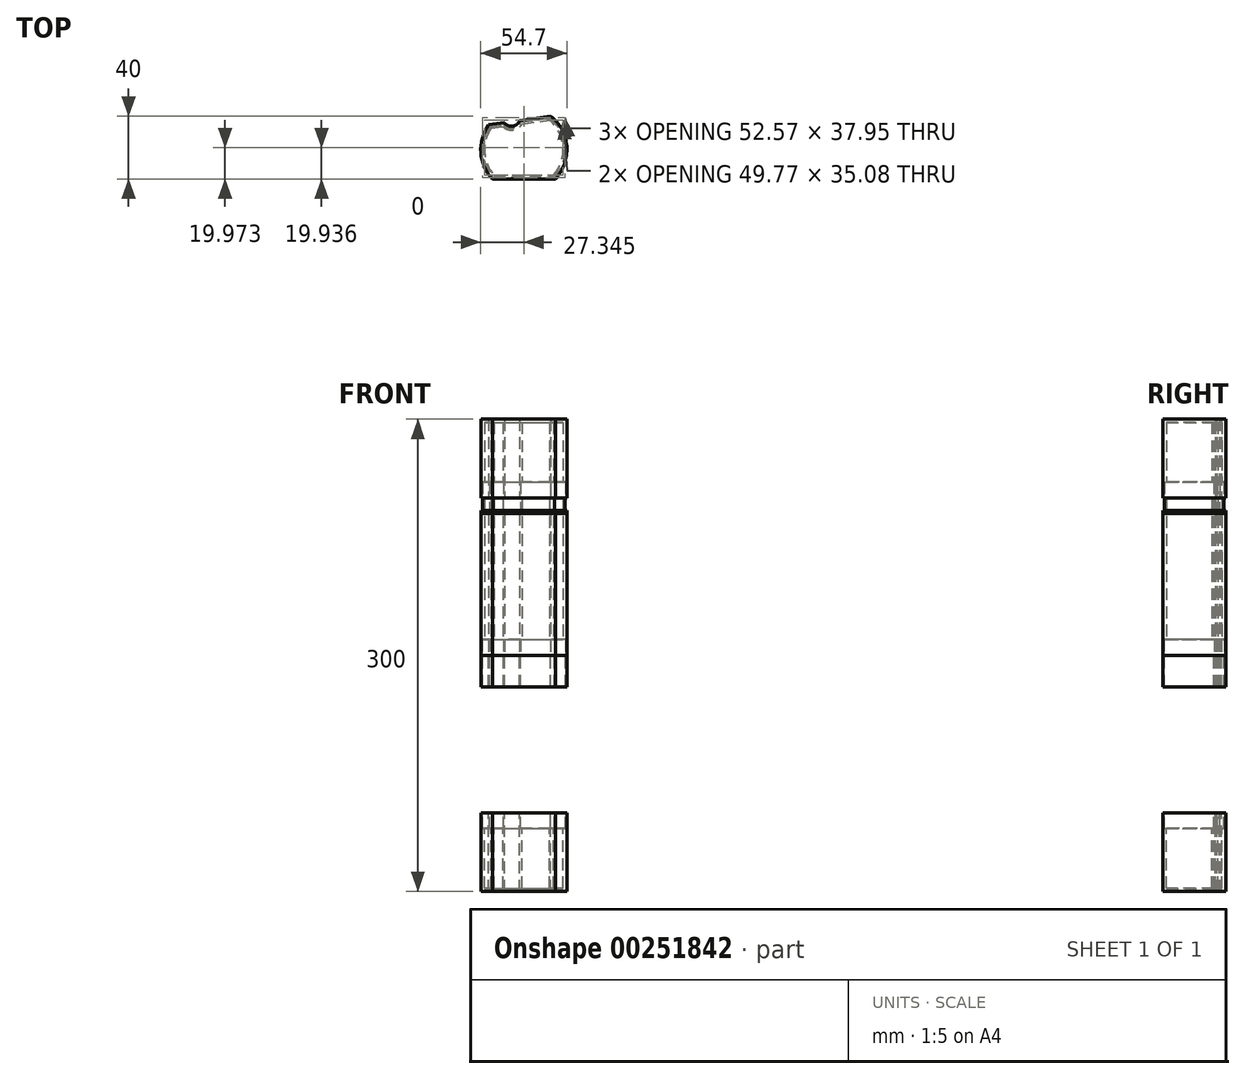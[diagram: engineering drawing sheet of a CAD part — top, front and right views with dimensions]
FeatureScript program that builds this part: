
annotation { "Feature Type Name" : "Feature", "Feature Type Description" : "" }
export const myFeature = defineFeature(function(context is Context, id is Id, definition is map)
    precondition{}
    {
        {
            var Q0;
            Q0=qCreatedBy(makeId("Top.planeOp"),FACE);
            var sketch = newSketch(context, id + "F0", { "sketchPlane" : qUnion([Q0])});
            skArc(sketch, "E0", {"start": v(27.91, -15.73) * mm, "mid": v(35.19, 4.9) * mm, "end": v(25, 24.27) * mm});
            skArc(sketch, "E1.trimOffspring", {"start": v(-14.4, 18.73) * mm, "mid": v(-19.38, 1.09) * mm, "end": v(-12.09, -15.73) * mm});
            skLineSegment(sketch, "E2", {"start": v(-14.4, 18.73) * mm, "end": v(-4.5, 20.12) * mm});
            skLineSegment(sketch, "E3.trimOffspring", {"start": v(27.91, -15.73) * mm, "end": v(27.91, -15.73) * mm});
            skLineSegment(sketch, "E4", {"start": v(-12.09, -15.73) * mm, "end": v(27.91, -15.73) * mm});
            skArc(sketch, "E5", {"start": v(-4.5, 20.12) * mm, "mid": v(0.77, 17.83) * mm, "end": v(5.2, 21.49) * mm});
            skLineSegment(sketch, "E6.trimOffspring", {"start": v(5.2, 21.49) * mm, "end": v(25, 24.27) * mm});
            skLineSegment(sketch, "E7.0", {"start": v(-13.02, 16.5) * mm, "end": v(-5.45, 17.56) * mm});
            skLineSegment(sketch, "E7.1", {"start": v(-11.02, -13.33) * mm, "end": v(26.84, -13.33) * mm});
            skArc(sketch, "E7.2", {"start": v(26.84, -13.33) * mm, "mid": v(32.8, 4.73) * mm, "end": v(24.28, 21.74) * mm});
            skArc(sketch, "E7.3", {"start": v(-13.02, 16.5) * mm, "mid": v(-16.98, 1.25) * mm, "end": v(-11.02, -13.33) * mm});
            skLineSegment(sketch, "E7.4", {"start": v(6.82, 19.29) * mm, "end": v(24.28, 21.74) * mm});
            skArc(sketch, "E7.5", {"start": v(-5.45, 17.56) * mm, "mid": v(1.1, 15.46) * mm, "end": v(6.82, 19.29) * mm});
            skSolve(sketch);
        }
        {
            var Q0;
            Q0=makeQuery(id+"F0.imprint","IMPRINT",FACE,{"disambiguationData":[TD([[makeQuery(id+"F0.imprint","IMPRINT",EDGE,{"derivedFrom":sQuery(id+"F0.wireOp",EDGE,"E0")}),1.0]])]});
            extrude(context, id + "F1", {"entities" : qUnion([Q0]), "depth" : 100 * mm});
        }
        {
            var Q0;
            Q0=makeQuery(id+"F1.opExtrude","CAP_FACE",FACE,{"disambiguationData":[OSD([sQuery(id+"F0.wireOp",EDGE,"E0"),sQuery(id+"F0.wireOp",EDGE,"E1.trimOffspring"),sQuery(id+"F0.wireOp",EDGE,"E2"),sQuery(id+"F0.wireOp",EDGE,"E4"),sQuery(id+"F0.wireOp",EDGE,"E5"),sQuery(id+"F0.wireOp",EDGE,"E6.trimOffspring"),sQuery(id+"F0.wireOp",EDGE,"E7.0"),sQuery(id+"F0.wireOp",EDGE,"E7.1"),sQuery(id+"F0.wireOp",EDGE,"E7.2"),sQuery(id+"F0.wireOp",EDGE,"E7.3"),sQuery(id+"F0.wireOp",EDGE,"E7.4"),sQuery(id+"F0.wireOp",EDGE,"E7.5")])],"isStart":true});
            var sketch = newSketch(context, id + "F2", { "sketchPlane" : qUnion([Q0])});
            skArc(sketch, "E8.0", {"start": v(-4.86, -19.26) * mm, "mid": v(0.88, -17.04) * mm, "end": v(5.77, -20.76) * mm});
            skArc(sketch, "E8.1", {"start": v(27.56, 14.93) * mm, "mid": v(34.39, -4.85) * mm, "end": v(24.77, -23.43) * mm});
            skLineSegment(sketch, "E8.2", {"start": v(-11.74, 14.93) * mm, "end": v(27.56, 14.93) * mm});
            skLineSegment(sketch, "E8.3", {"start": v(5.77, -20.76) * mm, "end": v(24.77, -23.43) * mm});
            skArc(sketch, "E8.4", {"start": v(-13.95, -17.99) * mm, "mid": v(-18.58, -1.14) * mm, "end": v(-11.74, 14.93) * mm});
            skLineSegment(sketch, "E8.5", {"start": v(-13.95, -17.99) * mm, "end": v(-4.86, -19.26) * mm});
            skSolve(sketch);
        }
        {
            var Q0;
            Q0=makeQuery(id+"F2.imprint","IMPRINT",FACE,{"disambiguationData":[TD([[makeQuery(id+"F2.imprint","IMPRINT",EDGE,{"derivedFrom":sQuery(id+"F2.wireOp",EDGE,"E8.0")}),-1.0]])]});
            extrude(context, id + "F3", {"entities" : qUnion([Q0]), "operationType" : NewBodyOperationType.REMOVE, "oppositeDirection" : true, "depth" : 10 * mm});
        }
        {
            var Q0;
            Q0=makeQuery(id+"F1.opExtrude","CAP_FACE",FACE,{"disambiguationData":[OSD([sQuery(id+"F0.wireOp",EDGE,"E0"),sQuery(id+"F0.wireOp",EDGE,"E1.trimOffspring"),sQuery(id+"F0.wireOp",EDGE,"E2"),sQuery(id+"F0.wireOp",EDGE,"E4"),sQuery(id+"F0.wireOp",EDGE,"E5"),sQuery(id+"F0.wireOp",EDGE,"E6.trimOffspring"),sQuery(id+"F0.wireOp",EDGE,"E7.0"),sQuery(id+"F0.wireOp",EDGE,"E7.1"),sQuery(id+"F0.wireOp",EDGE,"E7.2"),sQuery(id+"F0.wireOp",EDGE,"E7.3"),sQuery(id+"F0.wireOp",EDGE,"E7.4"),sQuery(id+"F0.wireOp",EDGE,"E7.5")])],"isStart":false});
            var sketch = newSketch(context, id + "F4", { "sketchPlane" : qUnion([Q0])});
            skArc(sketch, "E9.0", {"start": v(-13.72, 17.61) * mm, "mid": v(-18.18, 1.17) * mm, "end": v(-11.56, -14.53) * mm});
            skArc(sketch, "E9.1", {"start": v(-5.02, 18.84) * mm, "mid": v(0.93, 16.64) * mm, "end": v(6.05, 20.4) * mm});
            skLineSegment(sketch, "E9.2", {"start": v(6.05, 20.4) * mm, "end": v(24.65, 23) * mm});
            skLineSegment(sketch, "E9.3", {"start": v(-13.72, 17.61) * mm, "end": v(-5.02, 18.84) * mm});
            skArc(sketch, "E9.4", {"start": v(27.38, -14.53) * mm, "mid": v(33.99, 4.82) * mm, "end": v(24.65, 23) * mm});
            skLineSegment(sketch, "E9.5", {"start": v(-11.56, -14.53) * mm, "end": v(27.38, -14.53) * mm});
            skSolve(sketch);
        }
        {
            var Q0;
            Q0=makeQuery(id+"F4.imprint","IMPRINT",FACE,{"disambiguationData":[TD([[makeQuery(id+"F4.imprint","IMPRINT",EDGE,{"derivedFrom":sQuery(id+"F4.wireOp",EDGE,"E9.0")}),-1.0]])]});
            extrude(context, id + "F5", {"entities" : qUnion([Q0]), "operationType" : NewBodyOperationType.REMOVE, "oppositeDirection" : true, "depth" : 10 * mm});
        }
        {
            var Q0;
            Q0=makeQuery(id+"F5.boolean.opBoolean","COPY",FACE,{"derivedFrom":makeQuery(id+"F5.opExtrude","CAP_FACE",FACE,{"disambiguationData":[OSD([sQuery(id+"F0.wireOp",EDGE,"E0"),sQuery(id+"F0.wireOp",EDGE,"E1.trimOffspring"),sQuery(id+"F0.wireOp",EDGE,"E2"),sQuery(id+"F0.wireOp",EDGE,"E4"),sQuery(id+"F0.wireOp",EDGE,"E5"),sQuery(id+"F0.wireOp",EDGE,"E6.trimOffspring"),sQuery(id+"F4.wireOp",EDGE,"E9.0"),sQuery(id+"F4.wireOp",EDGE,"E9.1"),sQuery(id+"F4.wireOp",EDGE,"E9.2"),sQuery(id+"F4.wireOp",EDGE,"E9.3"),sQuery(id+"F4.wireOp",EDGE,"E9.4"),sQuery(id+"F4.wireOp",EDGE,"E9.5")])],"isStart":false})});
            var sketch = newSketch(context, id + "F6", { "sketchPlane" : qUnion([Q0])});
            skArc(sketch, "E10.0", {"start": v(-14.4, 18.73) * mm, "mid": v(-19.38, 1.09) * mm, "end": v(-12.09, -15.73) * mm});
            skLineSegment(sketch, "E11.0", {"start": v(-14.4, 18.73) * mm, "end": v(-4.5, 20.12) * mm});
            skArc(sketch, "E12.0", {"start": v(-4.5, 20.12) * mm, "mid": v(0.77, 17.83) * mm, "end": v(5.2, 21.49) * mm});
            skLineSegment(sketch, "E13.0", {"start": v(5.2, 21.49) * mm, "end": v(25, 24.27) * mm});
            skArc(sketch, "E14.0", {"start": v(27.91, -15.73) * mm, "mid": v(35.19, 4.9) * mm, "end": v(25, 24.27) * mm});
            skLineSegment(sketch, "E15.0", {"start": v(-12.09, -15.73) * mm, "end": v(27.91, -15.73) * mm});
            skArc(sketch, "E16.0", {"start": v(-13.83, 17.8) * mm, "mid": v(-18.38, 1.16) * mm, "end": v(-11.65, -14.73) * mm});
            skArc(sketch, "E16.1", {"start": v(-4.94, 19.05) * mm, "mid": v(0.9, 16.84) * mm, "end": v(5.91, 20.58) * mm});
            skLineSegment(sketch, "E16.2", {"start": v(5.91, 20.58) * mm, "end": v(24.71, 23.22) * mm});
            skLineSegment(sketch, "E16.3", {"start": v(-13.83, 17.8) * mm, "end": v(-4.94, 19.05) * mm});
            skArc(sketch, "E16.4", {"start": v(27.47, -14.73) * mm, "mid": v(34.19, 4.83) * mm, "end": v(24.71, 23.22) * mm});
            skLineSegment(sketch, "E16.5", {"start": v(-11.65, -14.73) * mm, "end": v(27.47, -14.73) * mm});
            skLineSegment(sketch, "E17.0", {"start": v(24.71, 23.22) * mm, "end": v(5.91, 20.58) * mm});
            skLineSegment(sketch, "E17.1", {"start": v(-4.94, 19.05) * mm, "end": v(-13.83, 17.8) * mm});
            skArc(sketch, "E17.3", {"start": v(5.91, 20.58) * mm, "mid": v(0.9, 16.84) * mm, "end": v(-4.94, 19.05) * mm});
            skSolve(sketch);
        }
        {
            var Q0;
            Q0 = qSketchRegion(id + "F6", true);
            extrude(context, id + "F7", {"entities" : qUnion([Q0]), "depth" : 2 * mm, "offsetDistance" : 25 * mm});
        }
        {
            var Q0;
            Q0=makeQuery(id+"F1.opExtrude","CAP_FACE",FACE,{"disambiguationData":[OSD([sQuery(id+"F0.wireOp",EDGE,"E0"),sQuery(id+"F0.wireOp",EDGE,"E1.trimOffspring"),sQuery(id+"F0.wireOp",EDGE,"E2"),sQuery(id+"F0.wireOp",EDGE,"E4"),sQuery(id+"F0.wireOp",EDGE,"E5"),sQuery(id+"F0.wireOp",EDGE,"E6.trimOffspring"),sQuery(id+"F0.wireOp",EDGE,"E7.0"),sQuery(id+"F0.wireOp",EDGE,"E7.1"),sQuery(id+"F0.wireOp",EDGE,"E7.2"),sQuery(id+"F0.wireOp",EDGE,"E7.3"),sQuery(id+"F0.wireOp",EDGE,"E7.4"),sQuery(id+"F0.wireOp",EDGE,"E7.5")])],"isStart":false});
            var sketch = newSketch(context, id + "F8", { "sketchPlane" : qUnion([Q0])});
            skLineSegment(sketch, "E18.0", {"start": v(-13.02, 16.5) * mm, "end": v(-5.45, 17.56) * mm});
            skArc(sketch, "E19.0", {"start": v(-13.02, 16.5) * mm, "mid": v(-16.98, 1.25) * mm, "end": v(-11.02, -13.33) * mm});
            skArc(sketch, "E20.0", {"start": v(-5.45, 17.56) * mm, "mid": v(1.1, 15.46) * mm, "end": v(6.82, 19.29) * mm});
            skLineSegment(sketch, "E21.0", {"start": v(6.82, 19.29) * mm, "end": v(24.28, 21.74) * mm});
            skArc(sketch, "E22.0", {"start": v(26.84, -13.33) * mm, "mid": v(32.8, 4.73) * mm, "end": v(24.28, 21.74) * mm});
            skPoint(sketch, "E23.0", {"position": v(7.91, -13.33) * mm});
            skArc(sketch, "E24.0", {"start": v(-14.4, 18.73) * mm, "mid": v(-19.38, 1.09) * mm, "end": v(-12.09, -15.73) * mm});
            skLineSegment(sketch, "E25.0", {"start": v(-14.4, 18.73) * mm, "end": v(-4.5, 20.12) * mm});
            skArc(sketch, "E26.0", {"start": v(-4.5, 20.12) * mm, "mid": v(0.77, 17.83) * mm, "end": v(5.2, 21.49) * mm});
            skLineSegment(sketch, "E27.0", {"start": v(5.2, 21.49) * mm, "end": v(25, 24.27) * mm});
            skArc(sketch, "E28.0", {"start": v(27.91, -15.73) * mm, "mid": v(35.19, 4.9) * mm, "end": v(25, 24.27) * mm});
            skLineSegment(sketch, "E29.0", {"start": v(-12.09, -15.73) * mm, "end": v(27.91, -15.73) * mm});
            skLineSegment(sketch, "E30.0", {"start": v(-4.94, 19.05) * mm, "end": v(-13.83, 17.8) * mm});
            skArc(sketch, "E31.0", {"start": v(-13.83, 17.8) * mm, "mid": v(-18.38, 1.16) * mm, "end": v(-11.65, -14.73) * mm});
            skLineSegment(sketch, "E32.0", {"start": v(-11.65, -14.73) * mm, "end": v(27.47, -14.73) * mm});
            skArc(sketch, "E33.0", {"start": v(27.47, -14.73) * mm, "mid": v(34.19, 4.83) * mm, "end": v(24.71, 23.22) * mm});
            skLineSegment(sketch, "E34.0", {"start": v(24.71, 23.22) * mm, "end": v(5.91, 20.58) * mm});
            skArc(sketch, "E35.0", {"start": v(5.91, 20.58) * mm, "mid": v(0.9, 16.84) * mm, "end": v(-4.94, 19.05) * mm});
            skLineSegment(sketch, "E36.0", {"start": v(-11.02, -13.33) * mm, "end": v(26.84, -13.33) * mm});
            skSolve(sketch);
        }
        {
            var Q0;
            Q0=makeQuery(id+"F8.imprint","IMPRINT",FACE,{"disambiguationData":[TD([[makeQuery(id+"F8.imprint","IMPRINT",EDGE,{"derivedFrom":sQuery(id+"F8.wireOp",EDGE,"E30.0")}),1.0]])]});
            var Q1;
            Q1=makeQuery(id+"F8.imprint","IMPRINT",FACE,{"disambiguationData":[TD([[makeQuery(id+"F8.imprint","IMPRINT",EDGE,{"derivedFrom":sQuery(id+"F8.wireOp",EDGE,"E24.0")}),1.0]])]});
            var Q2;
            Q2=makeQuery(id+"F8.imprint","IMPRINT",FACE,{"disambiguationData":[TD([[makeQuery(id+"F8.imprint","IMPRINT",EDGE,{"derivedFrom":sQuery(id+"F8.wireOp",EDGE,"E18.0")}),1.0]])]});
            extrude(context, id + "F9", {"entities" : qUnion([Q0, Q1, Q2]), "depth" : 50 * mm, "offsetDistance" : 25 * mm});
        }
        {
            var Q0;
            Q0=makeQuery(id+"F8.imprint","IMPRINT",FACE,{"disambiguationData":[TD([[makeQuery(id+"F8.imprint","IMPRINT",EDGE,{"derivedFrom":sQuery(id+"F8.wireOp",EDGE,"E30.0")}),1.0]])]});
            var Q1;
            Q1=makeQuery(id+"F8.imprint","IMPRINT",FACE,{"disambiguationData":[TD([[makeQuery(id+"F8.imprint","IMPRINT",EDGE,{"derivedFrom":sQuery(id+"F8.wireOp",EDGE,"E18.0")}),1.0]])]});
            extrude(context, id + "F10", {"entities" : qUnion([Q0, Q1]), "operationType" : NewBodyOperationType.REMOVE, "depth" : 10 * mm, "offsetDistance" : 25 * mm});
        }
        {
            var Q0;
            Q0=makeQuery(id+"F8.imprint","IMPRINT",FACE,{"disambiguationData":[TD([[makeQuery(id+"F8.imprint","IMPRINT",EDGE,{"derivedFrom":sQuery(id+"F8.wireOp",EDGE,"E18.0")}),-1.0]])]});
            var Q1;
            Q1=makeQuery(id+"F9.opExtrude","CAP_FACE",FACE,{"disambiguationData":[OSD([sQuery(id+"F8.wireOp",EDGE,"E18.0"),sQuery(id+"F8.wireOp",EDGE,"E19.0"),sQuery(id+"F8.wireOp",EDGE,"E20.0"),sQuery(id+"F8.wireOp",EDGE,"E21.0"),sQuery(id+"F8.wireOp",EDGE,"E22.0"),sQuery(id+"F8.wireOp",EDGE,"E24.0"),sQuery(id+"F8.wireOp",EDGE,"E25.0"),sQuery(id+"F8.wireOp",EDGE,"E26.0"),sQuery(id+"F8.wireOp",EDGE,"E27.0"),sQuery(id+"F8.wireOp",EDGE,"E28.0"),sQuery(id+"F8.wireOp",EDGE,"E29.0"),sQuery(id+"F8.wireOp",EDGE,"E36.0")])],"isStart":false});
            var Q2;
            Q2=makeQuery(id+"F9.opExtrude","CAP_FACE",FACE,{"disambiguationData":[OSD([sQuery(id+"F8.wireOp",EDGE,"E18.0"),sQuery(id+"F8.wireOp",EDGE,"E19.0"),sQuery(id+"F8.wireOp",EDGE,"E20.0"),sQuery(id+"F8.wireOp",EDGE,"E21.0"),sQuery(id+"F8.wireOp",EDGE,"E22.0"),sQuery(id+"F8.wireOp",EDGE,"E24.0"),sQuery(id+"F8.wireOp",EDGE,"E25.0"),sQuery(id+"F8.wireOp",EDGE,"E26.0"),sQuery(id+"F8.wireOp",EDGE,"E27.0"),sQuery(id+"F8.wireOp",EDGE,"E28.0"),sQuery(id+"F8.wireOp",EDGE,"E29.0"),sQuery(id+"F8.wireOp",EDGE,"E36.0")])],"isStart":false});
            extrude(context, id + "F11", {"entities" : qUnion([Q0]), "operationType" : NewBodyOperationType.ADD, "endBound" : BoundingType.UP_TO_SURFACE, "depth" : 50 * mm, "endBoundEntityFace" : qUnion([Q1]), "offsetDistance" : 25 * mm, "hasSecondDirection" : true, "secondDirectionBound" : SecondDirectionBoundingType.UP_TO_SURFACE, "secondDirectionOppositeDirection" : false, "secondDirectionDepth" : -2 * mm, "secondDirectionBoundEntityFace" : qUnion([Q2]), "hasSecondDirectionOffset" : true, "secondDirectionOffsetDistance" : 2 * mm});
        }
        {
            var Q0;
            Q0=makeQuery(id+"F1.opExtrude","CAP_FACE",FACE,{"disambiguationData":[OSD([sQuery(id+"F0.wireOp",EDGE,"E0"),sQuery(id+"F0.wireOp",EDGE,"E1.trimOffspring"),sQuery(id+"F0.wireOp",EDGE,"E2"),sQuery(id+"F0.wireOp",EDGE,"E4"),sQuery(id+"F0.wireOp",EDGE,"E5"),sQuery(id+"F0.wireOp",EDGE,"E6.trimOffspring"),sQuery(id+"F0.wireOp",EDGE,"E7.0"),sQuery(id+"F0.wireOp",EDGE,"E7.1"),sQuery(id+"F0.wireOp",EDGE,"E7.2"),sQuery(id+"F0.wireOp",EDGE,"E7.3"),sQuery(id+"F0.wireOp",EDGE,"E7.4"),sQuery(id+"F0.wireOp",EDGE,"E7.5")])],"isStart":true});
            var sketch = newSketch(context, id + "F12", { "sketchPlane" : qUnion([Q0])});
            skArc(sketch, "E37.0", {"start": v(-14.4, -18.73) * mm, "mid": v(-19.38, -1.09) * mm, "end": v(-12.09, 15.73) * mm});
            skLineSegment(sketch, "E38.0", {"start": v(-12.09, 15.73) * mm, "end": v(27.91, 15.73) * mm});
            skArc(sketch, "E39.0", {"start": v(27.91, 15.73) * mm, "mid": v(35.19, -4.9) * mm, "end": v(25, -24.27) * mm});
            skLineSegment(sketch, "E40.0", {"start": v(-14.4, -18.73) * mm, "end": v(-4.5, -20.12) * mm});
            skArc(sketch, "E41.0", {"start": v(-4.5, -20.12) * mm, "mid": v(0.77, -17.83) * mm, "end": v(5.2, -21.49) * mm});
            skLineSegment(sketch, "E42.0", {"start": v(5.2, -21.49) * mm, "end": v(25, -24.27) * mm});
            skLineSegment(sketch, "E43.0", {"start": v(-4.94, -19.05) * mm, "end": v(-13.83, -17.8) * mm});
            skArc(sketch, "E44.0", {"start": v(-13.83, -17.8) * mm, "mid": v(-18.38, -1.16) * mm, "end": v(-11.65, 14.73) * mm});
            skArc(sketch, "E45.0", {"start": v(5.91, -20.58) * mm, "mid": v(0.9, -16.84) * mm, "end": v(-4.94, -19.05) * mm});
            skLineSegment(sketch, "E46.0", {"start": v(24.71, -23.22) * mm, "end": v(5.91, -20.58) * mm});
            skArc(sketch, "E47.0", {"start": v(27.47, 14.73) * mm, "mid": v(34.19, -4.83) * mm, "end": v(24.71, -23.22) * mm});
            skLineSegment(sketch, "E48.0", {"start": v(-11.65, 14.73) * mm, "end": v(27.47, 14.73) * mm});
            skSolve(sketch);
        }
        {
            var Q0;
            Q0 = qSketchRegion(id + "F12", true);
            extrude(context, id + "F13", {"entities" : qUnion([Q0]), "depth" : 20 * mm, "offsetDistance" : 25 * mm});
        }
        {
            var Q0;
            Q0=makeQuery(id+"F9.opExtrude","SWEPT_BODY",BODY,{"disambiguationData":[OSD([sQuery(id+"F8.wireOp",EDGE,"E18.0"),sQuery(id+"F8.wireOp",EDGE,"E19.0"),sQuery(id+"F8.wireOp",EDGE,"E20.0"),sQuery(id+"F8.wireOp",EDGE,"E21.0"),sQuery(id+"F8.wireOp",EDGE,"E22.0"),sQuery(id+"F8.wireOp",EDGE,"E24.0"),sQuery(id+"F8.wireOp",EDGE,"E25.0"),sQuery(id+"F8.wireOp",EDGE,"E26.0"),sQuery(id+"F8.wireOp",EDGE,"E27.0"),sQuery(id+"F8.wireOp",EDGE,"E28.0"),sQuery(id+"F8.wireOp",EDGE,"E29.0"),sQuery(id+"F8.wireOp",EDGE,"E36.0")])]});
            var Q1;
            Q1=qCreatedBy(makeId("Top.planeOp"),FACE);
            mirror(context, id + "F14", {"entities" : qUnion([Q0]), "mirrorPlane" : qUnion([Q1])});
        }
    });
